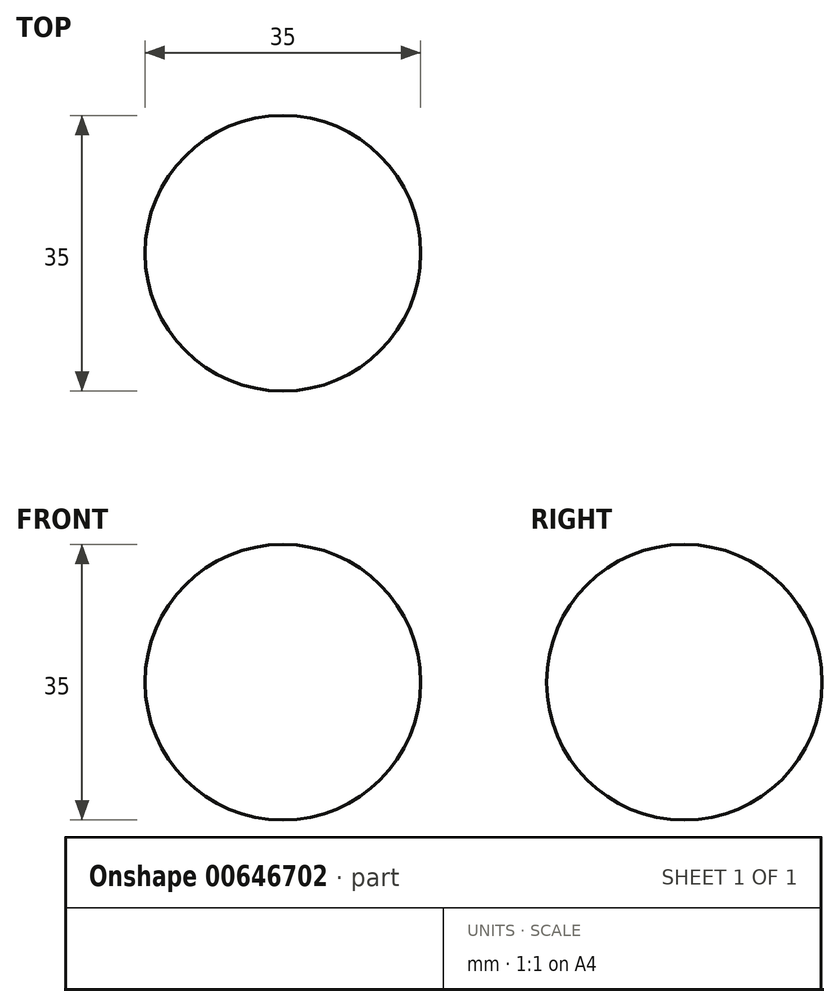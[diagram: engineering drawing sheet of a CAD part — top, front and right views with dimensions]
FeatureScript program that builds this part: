
annotation { "Feature Type Name" : "Feature", "Feature Type Description" : "" }
export const myFeature = defineFeature(function(context is Context, id is Id, definition is map)
    precondition{}
    {
        {
            var Q0;
            Q0=qCreatedBy(makeId("Front.planeOp"),FACE);
            var sketch = newSketch(context, id + "F0", { "sketchPlane" : qUnion([Q0])});
            skArc(sketch, "E0", {"start": v(0, -17.5) * mm, "mid": v(17.5, 0) * mm, "end": v(0, 17.5) * mm});
            skLineSegment(sketch, "E1", {"start": v(0, 17.5) * mm, "end": v(0, -17.5) * mm});
            skPoint(sketch, "E2.orphan", {"position": v(0, 17.27) * mm});
            skSolve(sketch);
        }
        {
            var Q0;
            {var subQ0=sQuery(id+"F0.wireOp",EDGE,"E0");Q0=makeQuery(id+"F0.imprint","IMPRINT",FACE,{"disambiguationData":[TD([[makeQuery(id+"F0.imprint","IMPRINT",EDGE,{"derivedFrom":subQ0}),1.0]])]});}
            var Q1;
            Q1=sQuery(id+"F0.wireOp",EDGE,"E1");
            revolve(context, id + "F1", {"entities" : qUnion([Q0]), "axis" : qUnion([Q1]), "revolveType" : RevolveType.FULL});
        }
    });
